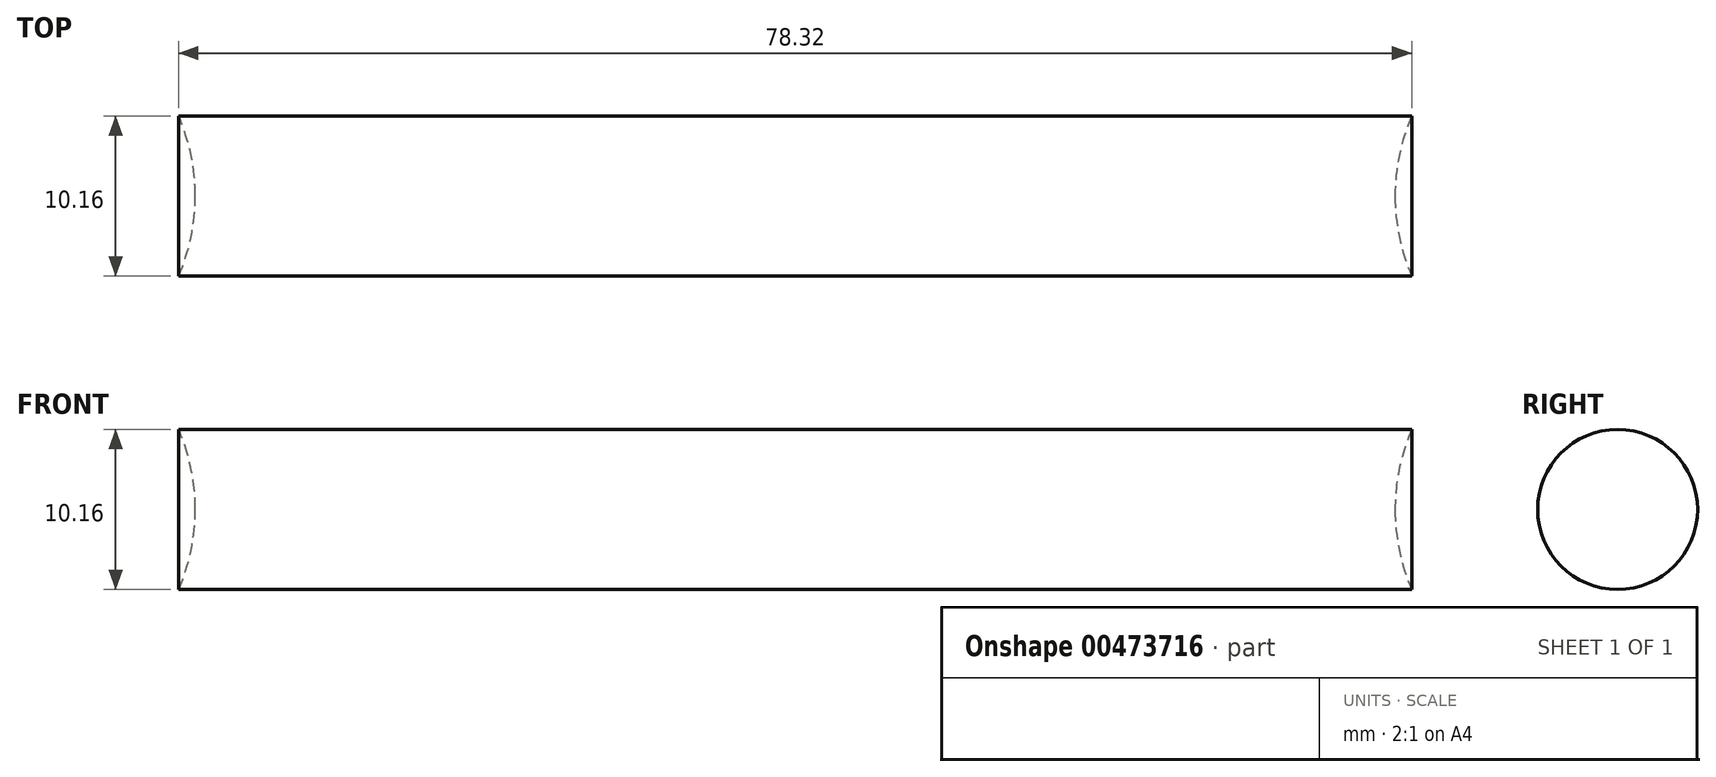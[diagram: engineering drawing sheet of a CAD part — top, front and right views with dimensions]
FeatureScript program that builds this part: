
annotation { "Feature Type Name" : "Feature", "Feature Type Description" : "" }
export const myFeature = defineFeature(function(context is Context, id is Id, definition is map)
    precondition{}
    {
        {
            var Q0;
            Q0=qCreatedBy(makeId("Front.planeOp"),FACE);
            var sketch = newSketch(context, id + "F0", { "sketchPlane" : qUnion([Q0])});
            skLineSegment(sketch, "E0", {"start": v(0, 0) * mm, "end": v(127, 0) * mm});
            skCircle(sketch, "E1", {"center": v(12.7, 0) * mm, "radius": 12.7 * mm});
            skCircle(sketch, "E2", {"center": v(114.3, 0) * mm, "radius": 12.7 * mm});
            skLineSegment(sketch, "E3", {"start": v(24.34, 5.08) * mm, "end": v(102.66, 5.08) * mm});
            skSolve(sketch);
        }
        {
            var Q0;
            {var subQ0=sQuery(id+"F0.wireOp",EDGE,"E1");var subQ1=sQuery(id+"F0.wireOp",EDGE,"E0");var subQ2=makeQuery(id+"F0.imprint","INTERSECT",VERTEX,{"disambiguationData":[OD(0.0)],"derivedFrom":[subQ1,subQ0]});Q0=makeQuery(id+"F0.imprint","IMPRINT",FACE,{"disambiguationData":[TD([[makeQuery(id+"F0.imprint","IMPRINT",EDGE,{"disambiguationData":[TD([[subQ2,-1.0]])],"derivedFrom":subQ1}),1.0]])]});}
            var Q1;
            {var subQ5=sQuery(id+"F0.wireOp",EDGE,"E3");Q1=makeQuery(id+"F0.imprint","IMPRINT",FACE,{"disambiguationData":[TD([[makeQuery(id+"F0.imprint","IMPRINT",EDGE,{"derivedFrom":subQ5}),-1.0]])]});}
            var Q2;
            Q2=sQuery(id+"F0.wireOp",EDGE,"E0");
            revolve(context, id + "F1", {"entities" : qUnion([Q0, Q1]), "axis" : qUnion([Q2]), "revolveType" : RevolveType.FULL});
        }
    });
